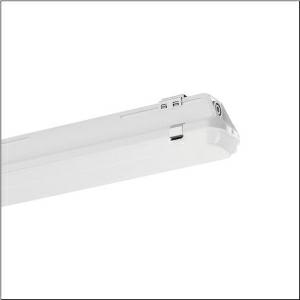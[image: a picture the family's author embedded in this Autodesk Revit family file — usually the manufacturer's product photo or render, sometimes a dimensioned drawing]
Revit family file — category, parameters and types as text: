
# Revit family: monsun_r__11_51fp20dp460l_ba2d
name_source: partatom
category: Lighting Fixtures
units: mm (PartAtom-declared; Revit-internal decimal feet)

## family parameters
Cut with Voids When Loaded = No
Host = Face
Light Source = No
Part Type = Normal
Room Calculation Point = No
Round Connector Dimension = Use Diameter
Shared = No

## types (1)
- --- (1 x LED, 5450 lm, 31.5 W, 4000K)
    Apparent Load = 32 VA
    CIE Flux Codes = 45 75 93 94 100
    Color Rendering = 80
    Color Temperature = 4000K
    Default Elevation = 1800 mm
    Description = Monsun® 11, damp-proof luminaire, chain hanger, primary optical cover: enclosure, of PC, light emission: direct distribution, primary light characteristic: symmetric, installation type: suspended mounting, surface-mounted, horizontal mounting, vertical mounting, LED, rated luminous flux: 5.450lm, luminous efficacy: 173lm/W, light colour: 840, colour temperature: 4000K, control gear: DALI 2, with terminal, 5-pole, max. 2.5mm², mains connection: 220..240V, AC, 50/60Hz, rated input power: 32W, luminaire housing, of glass-fibre reinforced polyester, uncoated, bright grey, incl. chain hanger, length: 1.590mm, width: 90mm, height: 88mm, clip for enclosure, of stainless steel (V2A), ceiling mounting element, of stainless steel (V2A), chain hanger, of stainless steel (V2A), protection rating (complete): IP66, insulation class (complete): insulation class I (protective earthing), certification: CE, ENEC, VDE, UKCA, protection symbol: D, impact resistance: IK08, permissible operating ambient temperature: -35..+40°C, standard: EN 50419, EN 60598-2-1, corresponds to IFS (International Featured Standards) requirements for safety and quality in the food industry, for indoor or canopied outdoor use, no direct snow, no direct sun, no direct rain, LABS conformity tested according to VDMA 24364:2018-05, contact your sales advisor before using the luminaires in applications with unclear chemical exposure, large temperature fluctuations or condensation-forming humidity, packaging unit: 1 piece
    Height = 89 mm
    Lamp = 1 x LED
    Lamp Light Flux = 5450 lm
    Lamp Power = 31.5 W
    Lamp count = 1
    Length = 1590 mm
    Luminous efficacy = 173 lm/W
    Manufacturer = Siteco
    ModVariant = No
    Model = 51FP20DP460L
    Mounting Place = Ceiling
    Mounting Type = Surface mounted
    Number of Poles = 1
    OnlyDefault = Yes
    Power Factor = 1
    Product Name = Monsun® 11
    Product group = damp-proof luminaire
    ProductGroupID = 301
    Protection Class = Protection class I
    Protection Degree = IP 66
    RLX_Detail_Level = 1
    RLX_Emergency_Light_Flux = 0 lm
    RLX_Emergency_Type = 0
    RLX_Emergency_Type_DB = No
    RlxData = <blob elided: 92301 chars, md5=5c517922>
    Socket = socket
    Standby Power = 0 W
    System Light Flux = 5450 lm
    System Power = 32 W
    Type Comments = factory setting: luminous flux: 100 % | dim-lin: 254 | 219 mA
    Type Image = l_1349237.jpg
    URL = http://relux.com
    VarID = @adj_038311
    Voltage = 0 V
    Weight = 0.00 kg
    Width = 90 mm

## geometry (parser evidence)
native form markers: Blend x4, Sweep x13
no freeform markers — native parametric forms only
